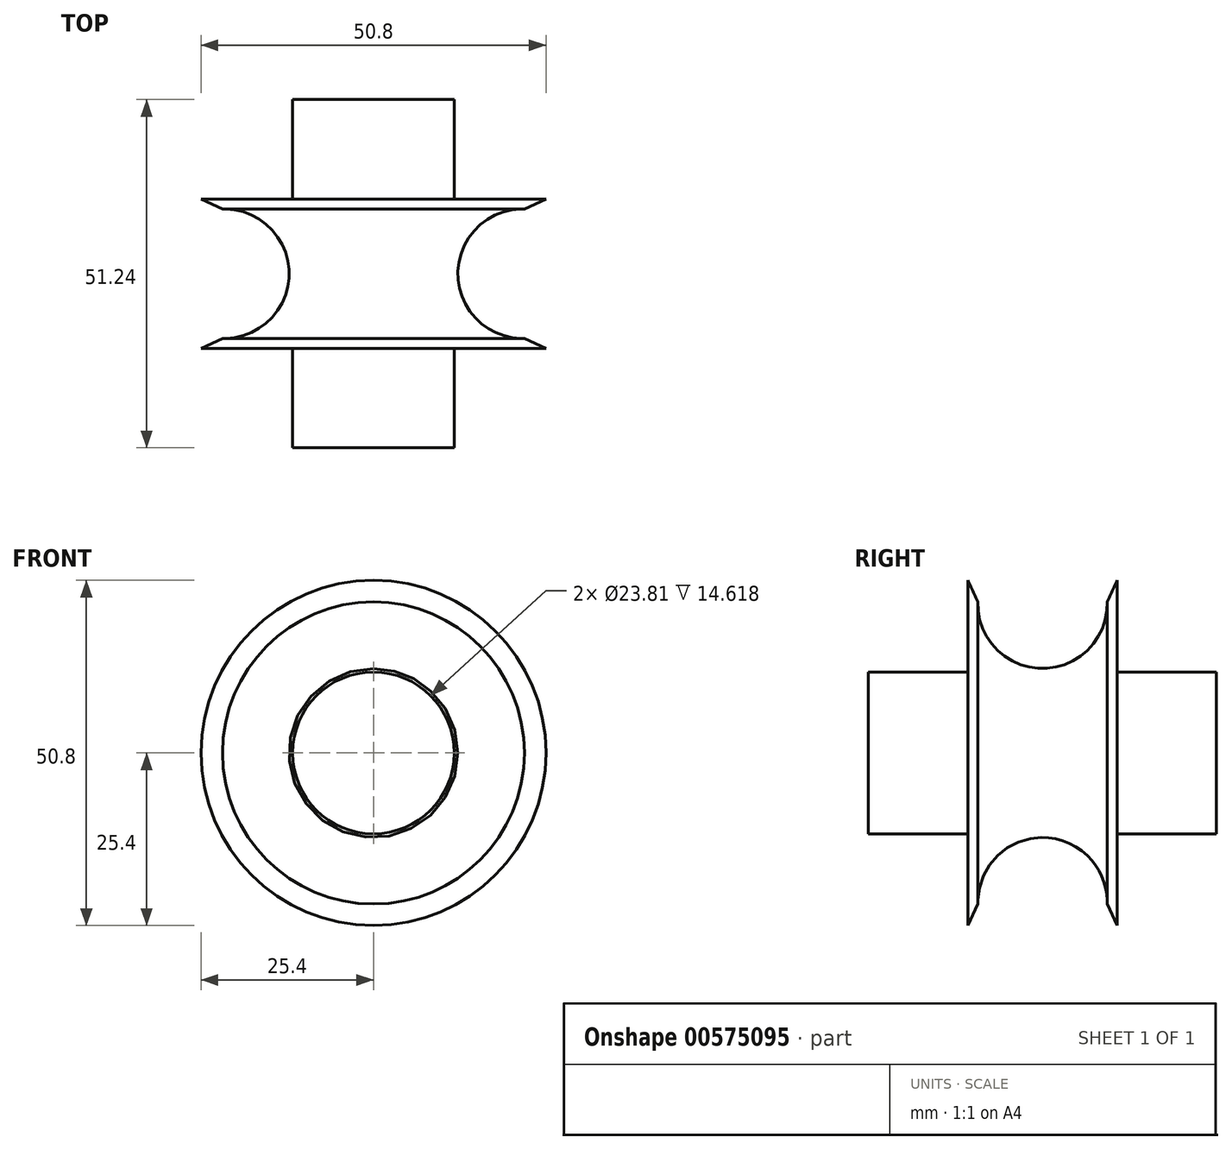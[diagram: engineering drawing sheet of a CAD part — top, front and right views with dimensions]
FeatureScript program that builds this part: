
annotation { "Feature Type Name" : "Feature", "Feature Type Description" : "" }
export const myFeature = defineFeature(function(context is Context, id is Id, definition is map)
    precondition{}
    {
        {
            var Q0;
            Q0=qCreatedBy(makeId("Right.planeOp"),FACE);
            var sketch = newSketch(context, id + "F0", { "sketchPlane" : qUnion([Q0])});
            skLineSegment(sketch, "E0", {"start": v(-76.33, 0) * mm, "end": v(59.75, 0) * mm, "construction": true});
            skLineSegment(sketch, "E1", {"start": v(-11, 11.9) * mm, "end": v(-25.62, 11.9) * mm});
            skLineSegment(sketch, "E2", {"start": v(-25.62, 11.9) * mm, "end": v(-25.62, 0) * mm});
            skLineSegment(sketch, "E3", {"start": v(11, 11.9) * mm, "end": v(25.62, 11.9) * mm});
            skLineSegment(sketch, "E4", {"start": v(25.62, 11.9) * mm, "end": v(25.62, 0) * mm});
            skLineSegment(sketch, "E5", {"start": v(-11, 25.4) * mm, "end": v(-9.52, 22.22) * mm});
            skLineSegment(sketch, "E6", {"start": v(11, 25.4) * mm, "end": v(9.52, 22.23) * mm});
            skArc(sketch, "E7", {"start": v(-9.52, 22.22) * mm, "mid": v(0, 12.43) * mm, "end": v(9.52, 22.23) * mm});
            skPoint(sketch, "E8", {"position": v(-11, 11.9) * mm});
            skPoint(sketch, "E9", {"position": v(11, 11.9) * mm});
            skLineSegment(sketch, "E10", {"start": v(-11, 11.9) * mm, "end": v(-11, 25.4) * mm});
            skLineSegment(sketch, "E11", {"start": v(11, 11.9) * mm, "end": v(11, 25.4) * mm});
            skSolve(sketch);
        }
        {
            var Q0;
            Q0=sQuery(id+"F0.wireOp",EDGE,"E7");
            var Q1;
            Q1=sQuery(id+"F0.wireOp",EDGE,"E5");
            var Q2;
            Q2=sQuery(id+"F0.wireOp",EDGE,"E6");
            var Q3;
            Q3=sQuery(id+"F0.wireOp",EDGE,"E1");
            var Q4;
            Q4=sQuery(id+"F0.wireOp",EDGE,"E3");
            var Q5;
            Q5=sQuery(id+"F0.wireOp",EDGE,"E2");
            var Q6;
            Q6=sQuery(id+"F0.wireOp",EDGE,"E4");
            var Q7;
            Q7=sQuery(id+"F0.wireOp",EDGE,"E10");
            var Q8;
            Q8=sQuery(id+"F0.wireOp",EDGE,"E11");
            var Q9;
            Q9=sQuery(id+"F0.wireOp",EDGE,"E0");
            revolve(context, id + "F1", {"bodyType" : ToolBodyType.SURFACE, "operationType" : NewBodyOperationType.ADD, "surfaceEntities" : qUnion([Q0, Q1, Q2, Q3, Q4, Q5, Q6, Q7, Q8]), "axis" : qUnion([Q9]), "revolveType" : RevolveType.FULL});
        }
    });
